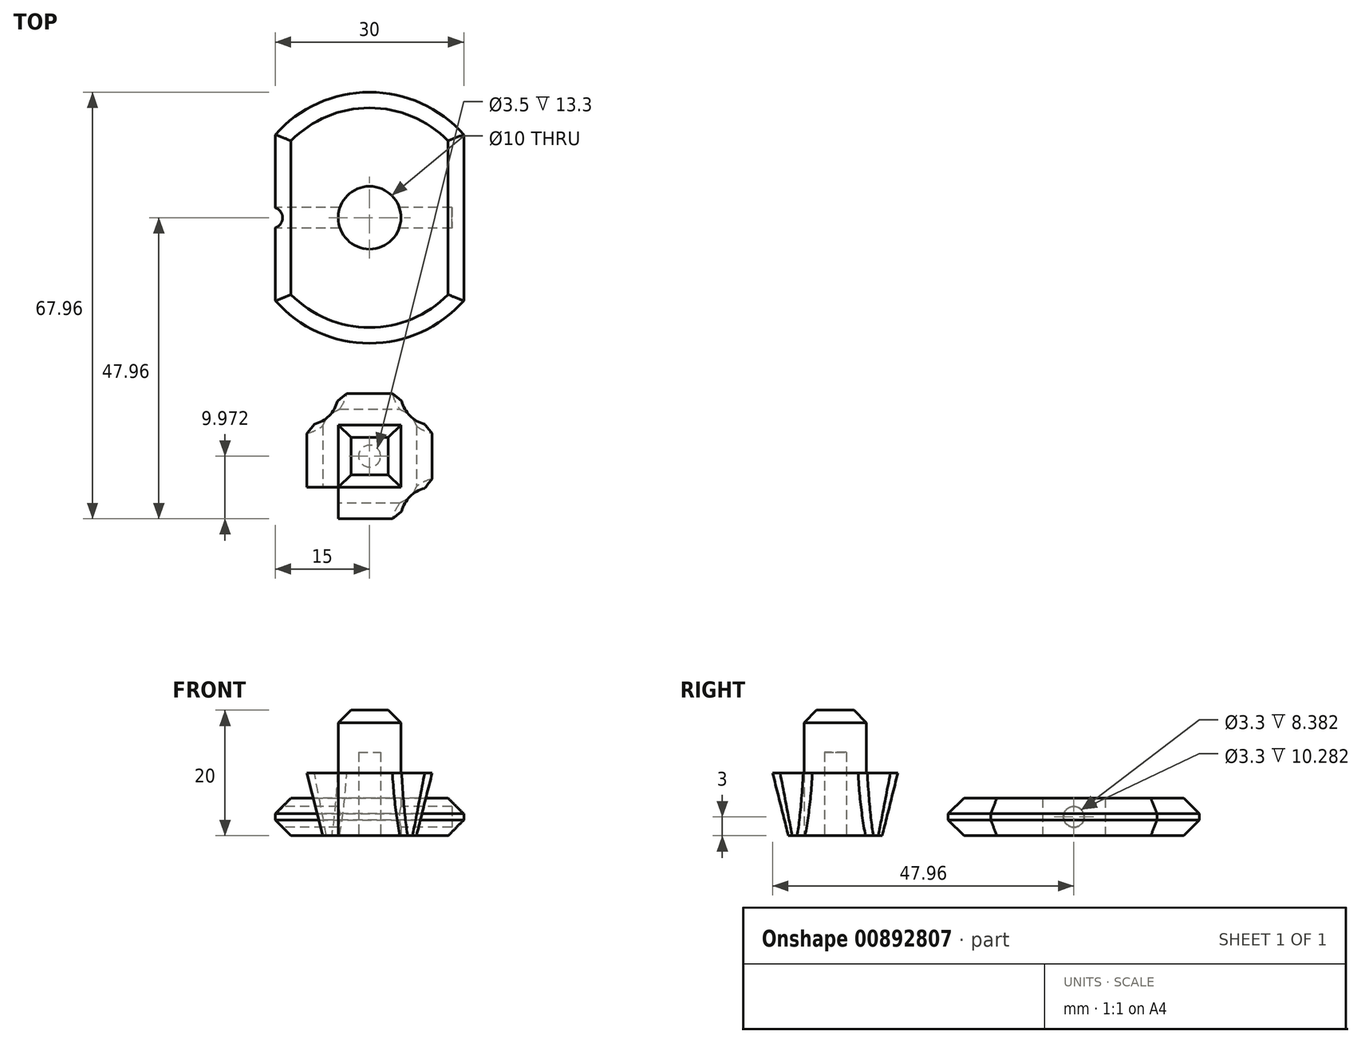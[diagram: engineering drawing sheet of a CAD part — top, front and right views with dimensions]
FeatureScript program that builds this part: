
annotation { "Feature Type Name" : "Feature", "Feature Type Description" : "" }
export const myFeature = defineFeature(function(context is Context, id is Id, definition is map)
    precondition{}
    {
        {
            var Q0;
            Q0=qCreatedBy(makeId("Top.planeOp"),FACE);
            var sketch = newSketch(context, id + "F0", { "sketchPlane" : qUnion([Q0])});
            skCircle(sketch, "E0", {"center": v(0, 0) * mm, "radius": 20 * mm});
            skCircle(sketch, "E1", {"center": v(0, 0) * mm, "radius": 5 * mm});
            skLineSegment(sketch, "E2", {"start": v(20, 0) * mm, "end": v(15, 0) * mm, "construction": true});
            skLineSegment(sketch, "E3", {"start": v(15, 0) * mm, "end": v(15, 13.23) * mm});
            skLineSegment(sketch, "E4", {"start": v(15, 0) * mm, "end": v(15, -13.23) * mm});
            skLineSegment(sketch, "E5.MirrorCS", {"start": v(-15, 0) * mm, "end": v(-15, 13.23) * mm});
            skLineSegment(sketch, "E6.MirrorCS", {"start": v(-15, 0) * mm, "end": v(-15, -13.23) * mm});
            skSolve(sketch);
        }
        {
            var Q0;
            Q0=makeQuery(id+"F0.imprint","IMPRINT",FACE,{"disambiguationData":[TD([[makeQuery(id+"F0.imprint","IMPRINT",EDGE,{"derivedFrom":sQuery(id+"F0.wireOp",EDGE,"E1")}),-1.0]])]});
            extrude(context, id + "F1", {"entities" : qUnion([Q0]), "depth" : 6 * mm, "offsetDistance" : 25 * mm});
        }
        {
            var Q0;
            Q0=makeQuery(id+"F1.opExtrude","SWEPT_FACE",FACE,{"disambiguationData":[OSD([sQuery(id+"F0.wireOp",EDGE,"E5.MirrorCS"),sQuery(id+"F0.wireOp",EDGE,"E6.MirrorCS")])]});
            var sketch = newSketch(context, id + "F2", { "sketchPlane" : qUnion([Q0])});
            skLineSegment(sketch, "E7", {"start": v(-13.23, 3) * mm, "end": v(13.23, 3) * mm, "construction": true});
            skLineSegment(sketch, "E8", {"start": v(0, 6) * mm, "end": v(0, 3) * mm, "construction": true});
            skCircle(sketch, "E9", {"center": v(0, 3) * mm, "radius": 1.65 * mm});
            skSolve(sketch);
        }
        {
            var Q0;
            Q0=makeQuery(id+"F2.imprint","IMPRINT",FACE,{"disambiguationData":[TD([[makeQuery(id+"F2.imprint","IMPRINT",EDGE,{"derivedFrom":sQuery(id+"F2.wireOp",EDGE,"E9")}),1.0]])]});
            extrude(context, id + "F3", {"entities" : qUnion([Q0]), "operationType" : NewBodyOperationType.REMOVE, "oppositeDirection" : true, "depth" : 28.1 * mm, "offsetDistance" : 25 * mm});
        }
        {
            var Q0;
            Q0=qCreatedBy(makeId("Top.planeOp"),FACE);
            var sketch = newSketch(context, id + "F4", { "sketchPlane" : qUnion([Q0])});
            skLineSegment(sketch, "E10.bottom", {"start": v(4.97, -42.96) * mm, "end": v(-4.97, -42.96) * mm});
            skLineSegment(sketch, "E10.top", {"start": v(4.97, -33.02) * mm, "end": v(-4.97, -33.02) * mm});
            skLineSegment(sketch, "E10.left", {"start": v(4.97, -42.96) * mm, "end": v(4.97, -33.02) * mm});
            skLineSegment(sketch, "E10.right", {"start": v(-4.97, -42.96) * mm, "end": v(-4.97, -33.02) * mm});
            skPoint(sketch, "E10.middle", {"position": v(0, -37.99) * mm});
            skSolve(sketch);
        }
        {
            var Q0;
            Q0=makeQuery(id+"F4.imprint","IMPRINT",FACE,{"disambiguationData":[TD([[makeQuery(id+"F4.imprint","IMPRINT",EDGE,{"derivedFrom":sQuery(id+"F4.wireOp",EDGE,"E10.bottom")}),-1.0]])]});
            extrude(context, id + "F5", {"entities" : qUnion([Q0]), "depth" : 20 * mm, "offsetDistance" : 25 * mm});
        }
        {
            var Q0;
            Q0=makeQuery(id+"F5.opExtrude","SWEPT_FACE",FACE,{"disambiguationData":[OSD([sQuery(id+"F4.wireOp",EDGE,"E10.right")])]});
            var sketch = newSketch(context, id + "F6", { "sketchPlane" : qUnion([Q0])});
            skLineSegment(sketch, "E11", {"start": v(33.02, 10) * mm, "end": v(42.96, 10) * mm});
            skSolve(sketch);
        }
        {
            var Q0;
            Q0 = qSketchRegion(id + "F6", true);
            var Q1;
            {var subQ0=sQuery(id+"F6.wireOp",EDGE,"E11");Q1=makeQuery(id+"F6.imprint","IMPRINT",FACE,{"disambiguationData":[TD([[makeQuery(id+"F6.imprint","IMPRINT",EDGE,{"derivedFrom":subQ0}),-1.0]])]});}
            extrude(context, id + "F7", {"entities" : qUnion([Q0, Q1]), "operationType" : NewBodyOperationType.ADD, "depth" : 5 * mm, "offsetDistance" : 25 * mm});
        }
        {
            var Q0;
            {var subQ0=sQuery(id+"F4.wireOp",EDGE,"E10.bottom");Q0=makeQuery(id+"F7.boolean.opBoolean","MERGE",FACE,{"derivedFrom":[makeQuery(id+"F5.opExtrude","SWEPT_FACE",FACE,{"disambiguationData":[OSD([subQ0])]}),makeQuery(id+"F7.opExtrude","SWEPT_FACE",FACE,{"disambiguationData":[OSD([subQ0,sQuery(id+"F4.wireOp",EDGE,"E10.right")])]})]});}
            var sketch = newSketch(context, id + "F8", { "sketchPlane" : qUnion([Q0])});
            skLineSegment(sketch, "E12", {"start": v(-4.97, 10) * mm, "end": v(-4.97, 0) * mm});
            skLineSegment(sketch, "E13", {"start": v(-9.97, 10) * mm, "end": v(-7.47, 0) * mm});
            skPoint(sketch, "E13.endSnap0", {"position": v(-7.47, 10) * mm});
            skSolve(sketch);
        }
        {
            var Q0;
            {var subQ0=sQuery(id+"F8.wireOp",EDGE,"E13");Q0=makeQuery(id+"F8.imprint","IMPRINT",FACE,{"disambiguationData":[TD([[makeQuery(id+"F8.imprint","IMPRINT",EDGE,{"derivedFrom":subQ0}),-1.0]])]});}
            extrude(context, id + "F9", {"entities" : qUnion([Q0]), "operationType" : NewBodyOperationType.REMOVE, "oppositeDirection" : true, "depth" : 10 * mm, "offsetDistance" : 25 * mm});
        }
        {
            var Q0;
            Q0=makeQuery(id+"F5.opExtrude","SWEPT_FACE",FACE,{"disambiguationData":[OSD([sQuery(id+"F4.wireOp",EDGE,"E10.left")])]});
            var sketch = newSketch(context, id + "F10", { "sketchPlane" : qUnion([Q0])});
            skLineSegment(sketch, "E14", {"start": v(-33.02, 10) * mm, "end": v(-42.96, 10) * mm});
            skSolve(sketch);
        }
        {
            var Q0;
            {var subQ0=sQuery(id+"F10.wireOp",EDGE,"E14");Q0=makeQuery(id+"F10.imprint","IMPRINT",FACE,{"disambiguationData":[TD([[makeQuery(id+"F10.imprint","IMPRINT",EDGE,{"derivedFrom":subQ0}),1.0]])]});}
            extrude(context, id + "F11", {"entities" : qUnion([Q0]), "operationType" : NewBodyOperationType.ADD, "depth" : 5 * mm, "offsetDistance" : 25 * mm});
        }
        {
            var Q0;
            {var subQ0=sQuery(id+"F4.wireOp",EDGE,"E10.bottom");Q0=makeQuery(id+"F11.boolean.opBoolean","MERGE",FACE,{"derivedFrom":[makeQuery(id+"F7.boolean.opBoolean","MERGE",FACE,{"derivedFrom":[makeQuery(id+"F5.opExtrude","SWEPT_FACE",FACE,{"disambiguationData":[OSD([subQ0])]}),makeQuery(id+"F7.opExtrude","SWEPT_FACE",FACE,{"disambiguationData":[OSD([subQ0,sQuery(id+"F4.wireOp",EDGE,"E10.right")])]})]}),makeQuery(id+"F11.opExtrude","SWEPT_FACE",FACE,{"disambiguationData":[OSD([subQ0,sQuery(id+"F4.wireOp",EDGE,"E10.left")])]})]});}
            var sketch = newSketch(context, id + "F12", { "sketchPlane" : qUnion([Q0])});
            skLineSegment(sketch, "E15", {"start": v(4.97, 10) * mm, "end": v(4.97, 0) * mm});
            skLineSegment(sketch, "E16", {"start": v(4.97, 0) * mm, "end": v(9.97, 0) * mm});
            skLineSegment(sketch, "E17", {"start": v(9.97, 10) * mm, "end": v(7.47, 0) * mm});
            skSolve(sketch);
        }
        {
            var Q0;
            {var subQ2=sQuery(id+"F12.wireOp",EDGE,"E17");Q0=makeQuery(id+"F12.imprint","IMPRINT",FACE,{"disambiguationData":[TD([[makeQuery(id+"F12.imprint","IMPRINT",EDGE,{"derivedFrom":subQ2}),1.0]])]});}
            extrude(context, id + "F13", {"entities" : qUnion([Q0]), "operationType" : NewBodyOperationType.REMOVE, "oppositeDirection" : true, "depth" : 10 * mm, "offsetDistance" : 25 * mm});
        }
        {
            var Q0;
            {var subQ0=sQuery(id+"F4.wireOp",EDGE,"E10.bottom");Q0=makeQuery(id+"F11.boolean.opBoolean","MERGE",FACE,{"derivedFrom":[makeQuery(id+"F7.boolean.opBoolean","MERGE",FACE,{"derivedFrom":[makeQuery(id+"F5.opExtrude","SWEPT_FACE",FACE,{"disambiguationData":[OSD([subQ0])]}),makeQuery(id+"F7.opExtrude","SWEPT_FACE",FACE,{"disambiguationData":[OSD([subQ0,sQuery(id+"F4.wireOp",EDGE,"E10.right")])]})]}),makeQuery(id+"F11.opExtrude","SWEPT_FACE",FACE,{"disambiguationData":[OSD([subQ0,sQuery(id+"F4.wireOp",EDGE,"E10.left")])]})]});}
            var sketch = newSketch(context, id + "F14", { "sketchPlane" : qUnion([Q0])});
            skLineSegment(sketch, "E18", {"start": v(-4.97, 10) * mm, "end": v(-4.97, 0) * mm});
            skLineSegment(sketch, "E19", {"start": v(4.97, 10) * mm, "end": v(4.97, 0) * mm});
            skLineSegment(sketch, "E20", {"start": v(-4.97, 10) * mm, "end": v(4.97, 10) * mm});
            skLineSegment(sketch, "E21", {"start": v(-4.97, 0) * mm, "end": v(4.97, 0) * mm});
            skSolve(sketch);
        }
        {
            var Q0;
            Q0=makeQuery(id+"F14.imprint","IMPRINT",FACE,{"disambiguationData":[TD([[makeQuery(id+"F14.imprint","IMPRINT",EDGE,{"derivedFrom":sQuery(id+"F14.wireOp",EDGE,"E18")}),1.0]])]});
            extrude(context, id + "F15", {"entities" : qUnion([Q0]), "operationType" : NewBodyOperationType.ADD, "depth" : 5 * mm, "offsetDistance" : 25 * mm});
        }
        {
            var Q0;
            Q0=makeQuery(id+"F15.opExtrude","SWEPT_FACE",FACE,{"disambiguationData":[OSD([sQuery(id+"F14.wireOp",EDGE,"E18")])]});
            var sketch = newSketch(context, id + "F16", { "sketchPlane" : qUnion([Q0])});
            skLineSegment(sketch, "E22", {"start": v(47.96, 10) * mm, "end": v(45.46, 0) * mm});
            skSolve(sketch);
        }
        {
            var Q0;
            {var subQ0=sQuery(id+"F16.wireOp",EDGE,"E22");Q0=makeQuery(id+"F16.imprint","IMPRINT",FACE,{"disambiguationData":[TD([[makeQuery(id+"F16.imprint","IMPRINT",EDGE,{"derivedFrom":subQ0}),1.0]])]});}
            extrude(context, id + "F17", {"entities" : qUnion([Q0]), "operationType" : NewBodyOperationType.REMOVE, "oppositeDirection" : true, "depth" : 25 * mm, "offsetDistance" : 25 * mm});
        }
        {
            var Q0;
            {var subQ0=sQuery(id+"F4.wireOp",EDGE,"E10.top");Q0=makeQuery(id+"F11.boolean.opBoolean","MERGE",FACE,{"derivedFrom":[makeQuery(id+"F7.boolean.opBoolean","MERGE",FACE,{"derivedFrom":[makeQuery(id+"F5.opExtrude","SWEPT_FACE",FACE,{"disambiguationData":[OSD([subQ0])]}),makeQuery(id+"F7.opExtrude","SWEPT_FACE",FACE,{"disambiguationData":[OSD([subQ0,sQuery(id+"F4.wireOp",EDGE,"E10.right")])]})]}),makeQuery(id+"F11.opExtrude","SWEPT_FACE",FACE,{"disambiguationData":[OSD([subQ0,sQuery(id+"F4.wireOp",EDGE,"E10.left")])]})]});}
            var sketch = newSketch(context, id + "F18", { "sketchPlane" : qUnion([Q0])});
            skLineSegment(sketch, "E23", {"start": v(-4.97, 10) * mm, "end": v(4.97, 10) * mm});
            skLineSegment(sketch, "E24", {"start": v(-4.97, 10) * mm, "end": v(-4.97, 0) * mm});
            skLineSegment(sketch, "E25", {"start": v(4.97, 10) * mm, "end": v(4.97, 0) * mm});
            skLineSegment(sketch, "E26", {"start": v(4.97, 0) * mm, "end": v(-4.97, 0) * mm});
            skSolve(sketch);
        }
        {
            var Q0;
            Q0 = qSketchRegion(id + "F18", true);
            extrude(context, id + "F19", {"entities" : qUnion([Q0]), "operationType" : NewBodyOperationType.ADD, "depth" : 5 * mm, "offsetDistance" : 25 * mm});
        }
        {
            var Q0;
            Q0=makeQuery(id+"F19.opExtrude","SWEPT_FACE",FACE,{"disambiguationData":[OSD([sQuery(id+"F18.wireOp",EDGE,"E24")])]});
            var sketch = newSketch(context, id + "F20", { "sketchPlane" : qUnion([Q0])});
            skLineSegment(sketch, "E27", {"start": v(-28.02, 10) * mm, "end": v(-30.52, 0) * mm});
            skSolve(sketch);
        }
        {
            var Q0;
            {var subQ0=sQuery(id+"F20.wireOp",EDGE,"E27");Q0=makeQuery(id+"F20.imprint","IMPRINT",FACE,{"disambiguationData":[TD([[makeQuery(id+"F20.imprint","IMPRINT",EDGE,{"derivedFrom":subQ0}),1.0]])]});}
            extrude(context, id + "F21", {"entities" : qUnion([Q0]), "operationType" : NewBodyOperationType.REMOVE, "oppositeDirection" : true, "depth" : 25 * mm, "offsetDistance" : 25 * mm});
        }
        {
            var Q0;
            Q0=makeQuery(id+"F15.opExtrude","CAP_EDGE",EDGE,{"disambiguationData":[OSD([sQuery(id+"F14.wireOp",EDGE,"E18")])],"isStart":true});
            var Q1;
            Q1=makeQuery(id+"F15.opExtrude","CAP_EDGE",EDGE,{"disambiguationData":[OSD([sQuery(id+"F14.wireOp",EDGE,"E19")])],"isStart":true});
            var Q2;
            Q2=makeQuery(id+"F19.opExtrude","CAP_EDGE",EDGE,{"disambiguationData":[OSD([sQuery(id+"F18.wireOp",EDGE,"E24")])],"isStart":true});
            var Q3;
            Q3=makeQuery(id+"F19.opExtrude","CAP_EDGE",EDGE,{"disambiguationData":[OSD([sQuery(id+"F18.wireOp",EDGE,"E25")])],"isStart":true});
            fillet(context, id + "F22", {"entities" : qUnion([Q0, Q1, Q2, Q3]), "radius" : 5 * mm, "tangentPropagation" : true, "allowEdgeOverflow" : false});
        }
        {
            var Q0;
            Q0=makeQuery(id+"F5.opExtrude","CAP_FACE",FACE,{"disambiguationData":[OSD([sQuery(id+"F4.wireOp",EDGE,"E10.bottom"),sQuery(id+"F4.wireOp",EDGE,"E10.top"),sQuery(id+"F4.wireOp",EDGE,"E10.left"),sQuery(id+"F4.wireOp",EDGE,"E10.right")])],"isStart":false});
            chamfer(context, id + "F23", {"entities" : qUnion([Q0]), "width" : 2 * mm, "tangentPropagation" : true});
        }
        {
            var Q0;
            Q0=makeQuery(id+"F22.opFillet","BLEND_EDGE",EDGE,{"blendedFrom":[makeQuery(id+"F19.opExtrude","CAP_EDGE",EDGE,{"disambiguationData":[OSD([sQuery(id+"F18.wireOp",EDGE,"E25")])],"isStart":true}),makeQuery(id+"F21.boolean.opBoolean","COPY",FACE,{"derivedFrom":makeQuery(id+"F21.opExtrude","SWEPT_FACE",FACE,{"disambiguationData":[OSD([sQuery(id+"F20.wireOp",EDGE,"E27")])]})})],"blendedInto":[makeQuery(id+"F21.boolean.opBoolean","COPY",FACE,{"derivedFrom":makeQuery(id+"F21.opExtrude","SWEPT_FACE",FACE,{"disambiguationData":[OSD([sQuery(id+"F20.wireOp",EDGE,"E27")])]})})]});
            var Q1;
            Q1=makeQuery(id+"F22.opFillet","BLEND_EDGE",EDGE,{"blendedFrom":[makeQuery(id+"F19.opExtrude","CAP_EDGE",EDGE,{"disambiguationData":[OSD([sQuery(id+"F18.wireOp",EDGE,"E25")])],"isStart":true}),makeQuery(id+"F9.boolean.opBoolean","COPY",FACE,{"derivedFrom":makeQuery(id+"F9.opExtrude","SWEPT_FACE",FACE,{"disambiguationData":[OSD([sQuery(id+"F8.wireOp",EDGE,"E13")])]})})],"blendedInto":[makeQuery(id+"F9.boolean.opBoolean","COPY",FACE,{"derivedFrom":makeQuery(id+"F9.opExtrude","SWEPT_FACE",FACE,{"disambiguationData":[OSD([sQuery(id+"F8.wireOp",EDGE,"E13")])]})})]});
            var Q2;
            Q2=makeQuery(id+"F22.opFillet","BLEND_EDGE",EDGE,{"blendedFrom":[makeQuery(id+"F15.opExtrude","CAP_EDGE",EDGE,{"disambiguationData":[OSD([sQuery(id+"F14.wireOp",EDGE,"E18")])],"isStart":true}),makeQuery(id+"F9.boolean.opBoolean","COPY",FACE,{"derivedFrom":makeQuery(id+"F9.opExtrude","SWEPT_FACE",FACE,{"disambiguationData":[OSD([sQuery(id+"F8.wireOp",EDGE,"E13")])]})})],"blendedInto":[makeQuery(id+"F9.boolean.opBoolean","COPY",FACE,{"derivedFrom":makeQuery(id+"F9.opExtrude","SWEPT_FACE",FACE,{"disambiguationData":[OSD([sQuery(id+"F8.wireOp",EDGE,"E13")])]})})]});
            var Q3;
            Q3=makeQuery(id+"F22.opFillet","BLEND_EDGE",EDGE,{"blendedFrom":[makeQuery(id+"F15.opExtrude","CAP_EDGE",EDGE,{"disambiguationData":[OSD([sQuery(id+"F14.wireOp",EDGE,"E18")])],"isStart":true}),makeQuery(id+"F17.boolean.opBoolean","COPY",FACE,{"derivedFrom":makeQuery(id+"F17.opExtrude","SWEPT_FACE",FACE,{"disambiguationData":[OSD([sQuery(id+"F16.wireOp",EDGE,"E22")])]})})],"blendedInto":[makeQuery(id+"F17.boolean.opBoolean","COPY",FACE,{"derivedFrom":makeQuery(id+"F17.opExtrude","SWEPT_FACE",FACE,{"disambiguationData":[OSD([sQuery(id+"F16.wireOp",EDGE,"E22")])]})})]});
            var Q4;
            Q4=makeQuery(id+"F22.opFillet","BLEND_EDGE",EDGE,{"blendedFrom":[makeQuery(id+"F19.opExtrude","CAP_EDGE",EDGE,{"disambiguationData":[OSD([sQuery(id+"F18.wireOp",EDGE,"E24")])],"isStart":true}),makeQuery(id+"F21.boolean.opBoolean","COPY",FACE,{"derivedFrom":makeQuery(id+"F21.opExtrude","SWEPT_FACE",FACE,{"disambiguationData":[OSD([sQuery(id+"F20.wireOp",EDGE,"E27")])]})})],"blendedInto":[makeQuery(id+"F21.boolean.opBoolean","COPY",FACE,{"derivedFrom":makeQuery(id+"F21.opExtrude","SWEPT_FACE",FACE,{"disambiguationData":[OSD([sQuery(id+"F20.wireOp",EDGE,"E27")])]})})]});
            var Q5;
            Q5=makeQuery(id+"F22.opFillet","BLEND_EDGE",EDGE,{"blendedFrom":[makeQuery(id+"F19.opExtrude","CAP_EDGE",EDGE,{"disambiguationData":[OSD([sQuery(id+"F18.wireOp",EDGE,"E24")])],"isStart":true}),makeQuery(id+"F13.boolean.opBoolean","COPY",FACE,{"derivedFrom":makeQuery(id+"F13.opExtrude","SWEPT_FACE",FACE,{"disambiguationData":[OSD([sQuery(id+"F12.wireOp",EDGE,"E17")])]})})],"blendedInto":[makeQuery(id+"F13.boolean.opBoolean","COPY",FACE,{"derivedFrom":makeQuery(id+"F13.opExtrude","SWEPT_FACE",FACE,{"disambiguationData":[OSD([sQuery(id+"F12.wireOp",EDGE,"E17")])]})})]});
            var Q6;
            Q6=makeQuery(id+"F22.opFillet","BLEND_EDGE",EDGE,{"blendedFrom":[makeQuery(id+"F15.opExtrude","CAP_EDGE",EDGE,{"disambiguationData":[OSD([sQuery(id+"F14.wireOp",EDGE,"E19")])],"isStart":true}),makeQuery(id+"F13.boolean.opBoolean","COPY",FACE,{"derivedFrom":makeQuery(id+"F13.opExtrude","SWEPT_FACE",FACE,{"disambiguationData":[OSD([sQuery(id+"F12.wireOp",EDGE,"E17")])]})})],"blendedInto":[makeQuery(id+"F13.boolean.opBoolean","COPY",FACE,{"derivedFrom":makeQuery(id+"F13.opExtrude","SWEPT_FACE",FACE,{"disambiguationData":[OSD([sQuery(id+"F12.wireOp",EDGE,"E17")])]})})]});
            var Q7;
            Q7=makeQuery(id+"F22.opFillet","BLEND_EDGE",EDGE,{"blendedFrom":[makeQuery(id+"F15.opExtrude","CAP_EDGE",EDGE,{"disambiguationData":[OSD([sQuery(id+"F14.wireOp",EDGE,"E19")])],"isStart":true}),makeQuery(id+"F17.boolean.opBoolean","COPY",FACE,{"derivedFrom":makeQuery(id+"F17.opExtrude","SWEPT_FACE",FACE,{"disambiguationData":[OSD([sQuery(id+"F16.wireOp",EDGE,"E22")])]})})],"blendedInto":[makeQuery(id+"F17.boolean.opBoolean","COPY",FACE,{"derivedFrom":makeQuery(id+"F17.opExtrude","SWEPT_FACE",FACE,{"disambiguationData":[OSD([sQuery(id+"F16.wireOp",EDGE,"E22")])]})})]});
            chamfer(context, id + "F24", {"entities" : qUnion([Q0, Q1, Q2, Q3, Q4, Q5, Q6, Q7]), "width" : 1.5 * mm, "tangentPropagation" : true});
        }
        {
            var Q0;
            {var subQ0=sQuery(id+"F4.wireOp",EDGE,"E10.left");var subQ1=sQuery(id+"F4.wireOp",EDGE,"E10.right");Q0=makeQuery(id+"F19.boolean.opBoolean","MERGE",FACE,{"derivedFrom":[makeQuery(id+"F15.boolean.opBoolean","MERGE",FACE,{"derivedFrom":[makeQuery(id+"F11.boolean.opBoolean","MERGE",FACE,{"derivedFrom":[makeQuery(id+"F7.boolean.opBoolean","MERGE",FACE,{"derivedFrom":[makeQuery(id+"F5.opExtrude","CAP_FACE",FACE,{"disambiguationData":[OSD([sQuery(id+"F4.wireOp",EDGE,"E10.bottom"),sQuery(id+"F4.wireOp",EDGE,"E10.top"),subQ0,subQ1])],"isStart":true}),makeQuery(id+"F7.opExtrude","SWEPT_FACE",FACE,{"disambiguationData":[OSD([subQ1])]})]}),makeQuery(id+"F11.opExtrude","SWEPT_FACE",FACE,{"disambiguationData":[OSD([subQ0])]})]}),makeQuery(id+"F15.opExtrude","SWEPT_FACE",FACE,{"disambiguationData":[OSD([sQuery(id+"F14.wireOp",EDGE,"E21")])]})]}),makeQuery(id+"F19.opExtrude","SWEPT_FACE",FACE,{"disambiguationData":[OSD([sQuery(id+"F18.wireOp",EDGE,"E26")])]})]});}
            var sketch = newSketch(context, id + "F25", { "sketchPlane" : qUnion([Q0])});
            skLineSegment(sketch, "E28", {"start": v(7.47, 37.99) * mm, "end": v(-7.47, 37.99) * mm, "construction": true});
            skLineSegment(sketch, "E29", {"start": v(0, 30.52) * mm, "end": v(0, 37.99) * mm, "construction": true});
            skCircle(sketch, "E30", {"center": v(0, 37.99) * mm, "radius": 1.75 * mm});
            skSolve(sketch);
        }
        {
            var Q0;
            Q0=makeQuery(id+"F25.imprint","IMPRINT",FACE,{"disambiguationData":[TD([[makeQuery(id+"F25.imprint","IMPRINT",EDGE,{"derivedFrom":sQuery(id+"F25.wireOp",EDGE,"E30")}),1.0]])]});
            extrude(context, id + "F26", {"entities" : qUnion([Q0]), "operationType" : NewBodyOperationType.REMOVE, "oppositeDirection" : true, "depth" : 13.3 * mm, "offsetDistance" : 25 * mm});
        }
        {
            var Q0;
            {var subQ0=sQuery(id+"F0.wireOp",EDGE,"E0");Q0=makeQuery(id+"F1.opExtrude","CAP_EDGE",EDGE,{"disambiguationData":[OSD([subQ0]),TDD([makeQuery(id+"F0.imprint","IMPRINT",EDGE,{"disambiguationData":[TD([[makeQuery(id+"F0.imprint","INTERSECT",VERTEX,{"derivedFrom":[subQ0,sQuery(id+"F0.wireOp",EDGE,"E3")]}),-1.0]])],"derivedFrom":subQ0})])],"isStart":false});}
            var Q1;
            {var subQ0=sQuery(id+"F0.wireOp",EDGE,"E0");Q1=makeQuery(id+"F1.opExtrude","CAP_EDGE",EDGE,{"disambiguationData":[OSD([subQ0]),TDD([makeQuery(id+"F0.imprint","IMPRINT",EDGE,{"disambiguationData":[TD([[makeQuery(id+"F0.imprint","INTERSECT",VERTEX,{"derivedFrom":[subQ0,sQuery(id+"F0.wireOp",EDGE,"E4")]}),1.0]])],"derivedFrom":subQ0})])],"isStart":false});}
            var Q2;
            {var subQ0=sQuery(id+"F0.wireOp",EDGE,"E0");Q2=makeQuery(id+"F1.opExtrude","CAP_EDGE",EDGE,{"disambiguationData":[OSD([subQ0]),TDD([makeQuery(id+"F0.imprint","IMPRINT",EDGE,{"disambiguationData":[TD([[makeQuery(id+"F0.imprint","INTERSECT",VERTEX,{"derivedFrom":[subQ0,sQuery(id+"F0.wireOp",EDGE,"E3")]}),-1.0]])],"derivedFrom":subQ0})])],"isStart":true});}
            var Q3;
            {var subQ0=sQuery(id+"F0.wireOp",EDGE,"E0");Q3=makeQuery(id+"F1.opExtrude","CAP_EDGE",EDGE,{"disambiguationData":[OSD([subQ0]),TDD([makeQuery(id+"F0.imprint","IMPRINT",EDGE,{"disambiguationData":[TD([[makeQuery(id+"F0.imprint","INTERSECT",VERTEX,{"derivedFrom":[subQ0,sQuery(id+"F0.wireOp",EDGE,"E4")]}),1.0]])],"derivedFrom":subQ0})])],"isStart":true});}
            var Q4;
            Q4=makeQuery(id+"F1.opExtrude","CAP_EDGE",EDGE,{"disambiguationData":[OSD([sQuery(id+"F0.wireOp",EDGE,"E5.MirrorCS"),sQuery(id+"F0.wireOp",EDGE,"E6.MirrorCS")])],"isStart":false});
            var Q5;
            Q5=makeQuery(id+"F1.opExtrude","CAP_EDGE",EDGE,{"disambiguationData":[OSD([sQuery(id+"F0.wireOp",EDGE,"E5.MirrorCS"),sQuery(id+"F0.wireOp",EDGE,"E6.MirrorCS")])],"isStart":true});
            var Q6;
            Q6=makeQuery(id+"F1.opExtrude","CAP_EDGE",EDGE,{"disambiguationData":[OSD([sQuery(id+"F0.wireOp",EDGE,"E3"),sQuery(id+"F0.wireOp",EDGE,"E4")])],"isStart":false});
            var Q7;
            Q7=makeQuery(id+"F1.opExtrude","CAP_EDGE",EDGE,{"disambiguationData":[OSD([sQuery(id+"F0.wireOp",EDGE,"E3"),sQuery(id+"F0.wireOp",EDGE,"E4")])],"isStart":true});
            chamfer(context, id + "F27", {"entities" : qUnion([Q0, Q1, Q2, Q3, Q4, Q5, Q6, Q7]), "width" : 2.5 * mm, "tangentPropagation" : true});
        }
    });
